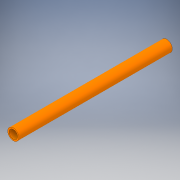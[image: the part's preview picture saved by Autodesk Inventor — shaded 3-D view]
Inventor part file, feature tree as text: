
AUTODESK INVENTOR PART (.ipt)
format: ipt  version: 2018.2 (Build 222227000, 227)  size: 106,496 bytes
history: native  units: in
note: dims shown in document units (in); Inventor stores cm internally (conversion verified against a paired STEP export)
features: extrude x1, sketch x1
ambient origin geometry x8: Origin, YZ Plane, XZ Plane, XY Plane, X Axis, Y Axis, Z Axis, Center Point
bodies: Solid1 (feature_tree)
feature tree (2):
  extrude  "Extrusion1"  Depth=18.0in
  sketch  "Sketch1"  dims[d0=1.315in d1=1.0in d2=18.0in d3=0.0in]
